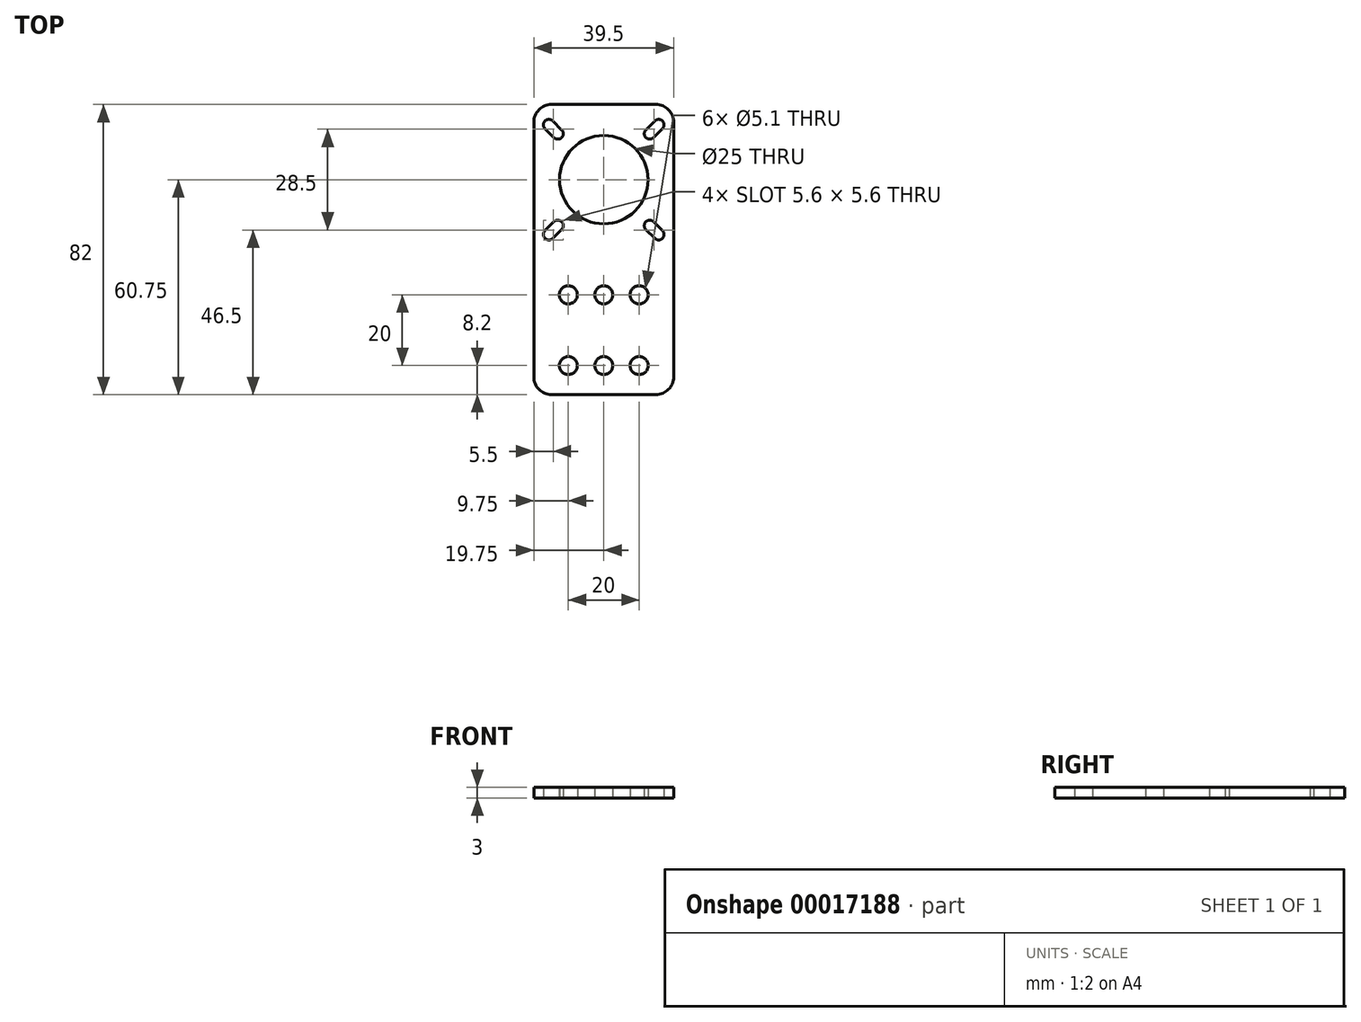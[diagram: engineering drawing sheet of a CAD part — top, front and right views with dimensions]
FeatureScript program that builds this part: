
annotation { "Feature Type Name" : "Feature", "Feature Type Description" : "" }
export const myFeature = defineFeature(function(context is Context, id is Id, definition is map)
    precondition{}
    {
        {
            var Q0;
            Q0=qCreatedBy(makeId("Top.planeOp"),FACE);
            var sketch = newSketch(context, id + "F0", { "sketchPlane" : qUnion([Q0])});
            skLineSegment(sketch, "E0.bottom", {"start": v(-14.75, 21.25) * mm, "end": v(14.75, 21.25) * mm});
            skLineSegment(sketch, "E0.top", {"start": v(-14.75, -60.75) * mm, "end": v(14.75, -60.75) * mm});
            skLineSegment(sketch, "E0.left", {"start": v(-19.75, 16.25) * mm, "end": v(-19.75, -55.75) * mm});
            skLineSegment(sketch, "E0.right", {"start": v(19.75, 16.25) * mm, "end": v(19.75, -55.75) * mm});
            skCircle(sketch, "E1", {"center": v(0, 0) * mm, "radius": 12.5 * mm});
            skPoint(sketch, "E2", {"position": v(0, 21.25) * mm});
            skCircle(sketch, "E3", {"center": v(0, -32.55) * mm, "radius": 2.55 * mm});
            skCircle(sketch, "E4", {"center": v(0, -52.55) * mm, "radius": 2.55 * mm});
            skCircle(sketch, "E5", {"center": v(10, -52.55) * mm, "radius": 2.55 * mm});
            skCircle(sketch, "E6", {"center": v(10, -32.55) * mm, "radius": 2.55 * mm});
            skLineSegment(sketch, "E7", {"start": v(0, -32.55) * mm, "end": v(14.81, -32.55) * mm, "construction": true});
            skLineSegment(sketch, "E8", {"start": v(0, -52.55) * mm, "end": v(17.38, -52.55) * mm, "construction": true});
            skLineSegment(sketch, "E9", {"start": v(0, -18.37) * mm, "end": v(0, -29.7) * mm, "construction": true});
            skCircle(sketch, "E10.MirrorC", {"center": v(-10, -52.55) * mm, "radius": 2.55 * mm});
            skCircle(sketch, "E11.MirrorC", {"center": v(-10, -32.55) * mm, "radius": 2.55 * mm});
            skLineSegment(sketch, "E12", {"start": v(0, 0) * mm, "end": v(21.76, 21.76) * mm, "construction": true});
            skPoint(sketch, "E13.visualSharp", {"position": v(-19.75, 21.25) * mm});
            skArc(sketch, "E13.filletArc", {"start": v(-14.75, 21.25) * mm, "mid": v(-18.29, 19.79) * mm, "end": v(-19.75, 16.25) * mm});
            skPoint(sketch, "E14.visualSharp", {"position": v(19.75, 21.25) * mm});
            skArc(sketch, "E14.filletArc", {"start": v(19.75, 16.25) * mm, "mid": v(18.29, 19.79) * mm, "end": v(14.75, 21.25) * mm});
            skPoint(sketch, "E15.visualSharp", {"position": v(19.75, -60.75) * mm});
            skArc(sketch, "E15.filletArc", {"start": v(14.75, -60.75) * mm, "mid": v(18.29, -59.29) * mm, "end": v(19.75, -55.75) * mm});
            skPoint(sketch, "E16.visualSharp", {"position": v(-19.75, -60.75) * mm});
            skArc(sketch, "E16.filletArc", {"start": v(-19.75, -55.75) * mm, "mid": v(-18.29, -59.29) * mm, "end": v(-14.75, -60.75) * mm});
            skArc(sketch, "E17", {"start": v(16.6, 14.4) * mm, "mid": v(16.6, 16.6) * mm, "end": v(14.4, 16.6) * mm});
            skArc(sketch, "E18", {"start": v(11.9, 14.1) * mm, "mid": v(11.9, 11.9) * mm, "end": v(14.1, 11.9) * mm});
            skLineSegment(sketch, "E19", {"start": v(10.29, 15.71) * mm, "end": v(14.32, 11.68) * mm, "construction": true});
            skLineSegment(sketch, "E20", {"start": v(14.01, 16.99) * mm, "end": v(17.22, 13.78) * mm, "construction": true});
            skLineSegment(sketch, "E21", {"start": v(11.9, 14.1) * mm, "end": v(14.4, 16.6) * mm});
            skLineSegment(sketch, "E22", {"start": v(14.1, 11.9) * mm, "end": v(16.6, 14.4) * mm});
            skArc(sketch, "E23.1.0", {"start": v(-14.1, 11.9) * mm, "mid": v(-11.9, 11.9) * mm, "end": v(-11.9, 14.1) * mm});
            skLineSegment(sketch, "E23.1.1", {"start": v(-14.1, 11.9) * mm, "end": v(-16.6, 14.4) * mm});
            skArc(sketch, "E23.1.2", {"start": v(-14.4, 16.6) * mm, "mid": v(-16.6, 16.6) * mm, "end": v(-16.6, 14.4) * mm});
            skLineSegment(sketch, "E23.1.3", {"start": v(-11.9, 14.1) * mm, "end": v(-14.4, 16.6) * mm});
            skArc(sketch, "E23.2.0", {"start": v(-11.9, -14.1) * mm, "mid": v(-11.9, -11.9) * mm, "end": v(-14.1, -11.9) * mm});
            skLineSegment(sketch, "E23.2.1", {"start": v(-11.9, -14.1) * mm, "end": v(-14.4, -16.6) * mm});
            skArc(sketch, "E23.2.2", {"start": v(-16.6, -14.4) * mm, "mid": v(-16.6, -16.6) * mm, "end": v(-14.4, -16.6) * mm});
            skLineSegment(sketch, "E23.2.3", {"start": v(-14.1, -11.9) * mm, "end": v(-16.6, -14.4) * mm});
            skArc(sketch, "E23.3.0", {"start": v(14.1, -11.9) * mm, "mid": v(11.9, -11.9) * mm, "end": v(11.9, -14.1) * mm});
            skLineSegment(sketch, "E23.3.1", {"start": v(14.1, -11.9) * mm, "end": v(16.6, -14.4) * mm});
            skArc(sketch, "E23.3.2", {"start": v(14.4, -16.6) * mm, "mid": v(16.6, -16.6) * mm, "end": v(16.6, -14.4) * mm});
            skLineSegment(sketch, "E23.3.3", {"start": v(11.9, -14.1) * mm, "end": v(14.4, -16.6) * mm});
            skSolve(sketch);
        }
        {
            var Q0;
            Q0 = qSketchRegion(id + "F0", true);
            extrude(context, id + "F1", {"entities" : qUnion([Q0]), "depth" : 3 * mm});
        }
    });
